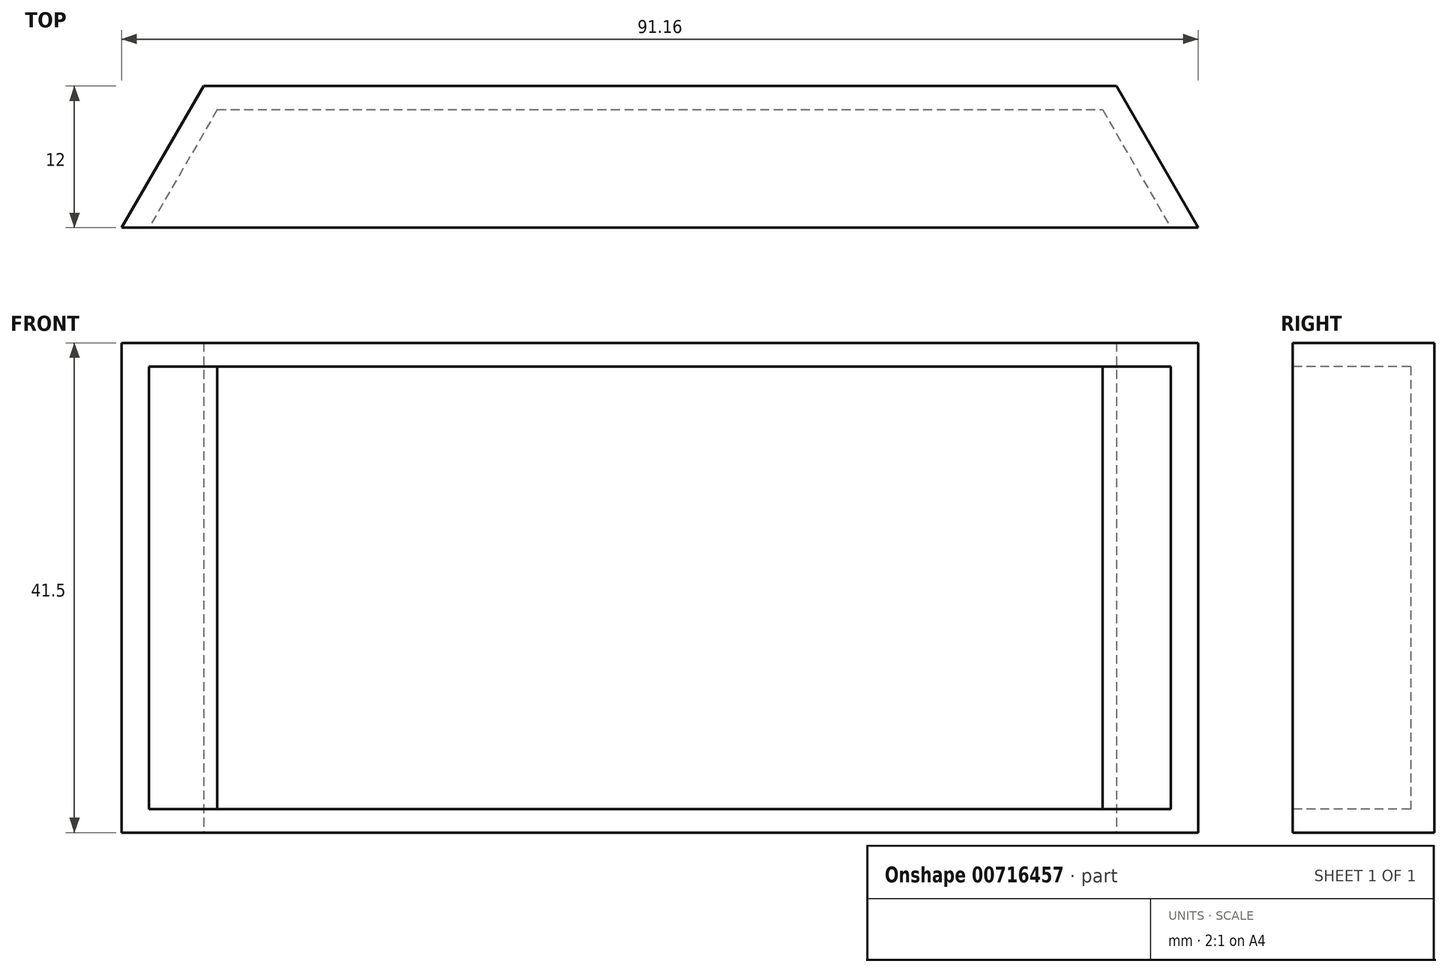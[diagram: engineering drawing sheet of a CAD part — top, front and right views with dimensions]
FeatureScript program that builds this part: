
annotation { "Feature Type Name" : "Feature", "Feature Type Description" : "" }
export const myFeature = defineFeature(function(context is Context, id is Id, definition is map)
    precondition{}
    {
        {
            var Q0;
            Q0=qCreatedBy(makeId("Top.planeOp"),FACE);
            var sketch = newSketch(context, id + "F0", { "sketchPlane" : qUnion([Q0])});
            skLineSegment(sketch, "E0.bottom", {"start": v(-37.5, 5) * mm, "end": v(37.5, 5) * mm});
            skPoint(sketch, "E0.middle", {"position": v(0, 0) * mm});
            skLineSegment(sketch, "E1", {"start": v(37.5, 5) * mm, "end": v(43.27, -5) * mm});
            skLineSegment(sketch, "E2.MirrorCS", {"start": v(-37.5, 5) * mm, "end": v(-43.27, -5) * mm});
            skLineSegment(sketch, "E3.2", {"start": v(38.65, 7) * mm, "end": v(45.58, -5) * mm});
            skLineSegment(sketch, "E3.3", {"start": v(-38.65, 7) * mm, "end": v(38.65, 7) * mm});
            skLineSegment(sketch, "E3.4", {"start": v(-38.65, 7) * mm, "end": v(-45.58, -5) * mm});
            skLineSegment(sketch, "E4", {"start": v(-43.27, -5) * mm, "end": v(-45.58, -5) * mm});
            skLineSegment(sketch, "E5", {"start": v(-45.58, -5) * mm, "end": v(-43.27, -5) * mm});
            skLineSegment(sketch, "E6", {"start": v(43.27, -5) * mm, "end": v(45.58, -5) * mm});
            skPoint(sketch, "E0.top.end.orphan", {"position": v(37.5, -5) * mm});
            skPoint(sketch, "E0.top.start.orphan", {"position": v(-37.5, -5) * mm});
            skPoint(sketch, "E7.MirrorCS.end.orphan", {"position": v(-43.27, -5) * mm});
            skSolve(sketch);
        }
        {
            var Q0;
            Q0=makeQuery(id+"F0.imprint","IMPRINT",FACE,{"disambiguationData":[TD([[makeQuery(id+"F0.imprint","IMPRINT",EDGE,{"derivedFrom":sQuery(id+"F0.wireOp",EDGE,"E0.bottom")}),1.0]])]});
            extrude(context, id + "F1", {"entities" : qUnion([Q0]), "depth" : 37.5 * mm, "offsetDistance" : 25 * mm});
        }
        {
            var Q0;
            Q0=makeQuery(id+"F1.opExtrude","CAP_FACE",FACE,{"disambiguationData":[OSD([sQuery(id+"F0.wireOp",EDGE,"E0.bottom"),sQuery(id+"F0.wireOp",EDGE,"E1"),sQuery(id+"F0.wireOp",EDGE,"E2.MirrorCS"),sQuery(id+"F0.wireOp",EDGE,"E3.2"),sQuery(id+"F0.wireOp",EDGE,"E3.3"),sQuery(id+"F0.wireOp",EDGE,"E3.4"),sQuery(id+"F0.wireOp",EDGE,"E5"),sQuery(id+"F0.wireOp",EDGE,"E6")])],"isStart":false});
            var sketch = newSketch(context, id + "F2", { "sketchPlane" : qUnion([Q0])});
            skLineSegment(sketch, "E8", {"start": v(-45.58, -5) * mm, "end": v(45.58, -5) * mm});
            skLineSegment(sketch, "E9", {"start": v(45.58, -5) * mm, "end": v(38.65, 7) * mm});
            skLineSegment(sketch, "E10", {"start": v(38.65, 7) * mm, "end": v(-38.65, 7) * mm});
            skLineSegment(sketch, "E11", {"start": v(-38.65, 7) * mm, "end": v(-45.58, -5) * mm});
            skSolve(sketch);
        }
        {
            var Q0;
            {var subQ0=sQuery(id+"F2.wireOp",EDGE,"E9");Q0=makeQuery(id+"F2.imprint","IMPRINT",FACE,{"disambiguationData":[TD([[makeQuery(id+"F2.imprint","IMPRINT",EDGE,{"derivedFrom":subQ0}),-1.0]])]});}
            var Q1;
            Q1=makeQuery(id+"F2.imprint","IMPRINT",FACE,{"disambiguationData":[TD([[makeQuery(id+"F2.imprint","IMPRINT",EDGE,{"derivedFrom":makeQuery(id+"F1.opExtrude","CAP_EDGE",EDGE,{"disambiguationData":[OSD([sQuery(id+"F0.wireOp",EDGE,"E0.bottom")])],"isStart":false})}),-1.0]])]});
            extrude(context, id + "F3", {"entities" : qUnion([Q0, Q1]), "operationType" : NewBodyOperationType.ADD, "depth" : 2 * mm, "offsetDistance" : 25 * mm});
        }
        {
            var Q0;
            Q0=makeQuery(id+"F1.opExtrude","CAP_FACE",FACE,{"disambiguationData":[OSD([sQuery(id+"F0.wireOp",EDGE,"E0.bottom"),sQuery(id+"F0.wireOp",EDGE,"E1"),sQuery(id+"F0.wireOp",EDGE,"E2.MirrorCS"),sQuery(id+"F0.wireOp",EDGE,"E3.2"),sQuery(id+"F0.wireOp",EDGE,"E3.3"),sQuery(id+"F0.wireOp",EDGE,"E3.4"),sQuery(id+"F0.wireOp",EDGE,"E5"),sQuery(id+"F0.wireOp",EDGE,"E6")])],"isStart":true});
            var sketch = newSketch(context, id + "F4", { "sketchPlane" : qUnion([Q0])});
            skLineSegment(sketch, "E12", {"start": v(-45.58, 5) * mm, "end": v(45.58, 5) * mm});
            skLineSegment(sketch, "E13", {"start": v(45.58, 5) * mm, "end": v(38.65, -7) * mm});
            skLineSegment(sketch, "E14", {"start": v(38.65, -7) * mm, "end": v(-38.65, -7) * mm});
            skLineSegment(sketch, "E15", {"start": v(-38.65, -7) * mm, "end": v(-45.58, 5) * mm});
            skSolve(sketch);
        }
        {
            var Q0;
            Q0 = qSketchRegion(id + "F4", true);
            extrude(context, id + "F5", {"entities" : qUnion([Q0]), "operationType" : NewBodyOperationType.ADD, "depth" : 2 * mm, "offsetDistance" : 25 * mm});
        }
    });
